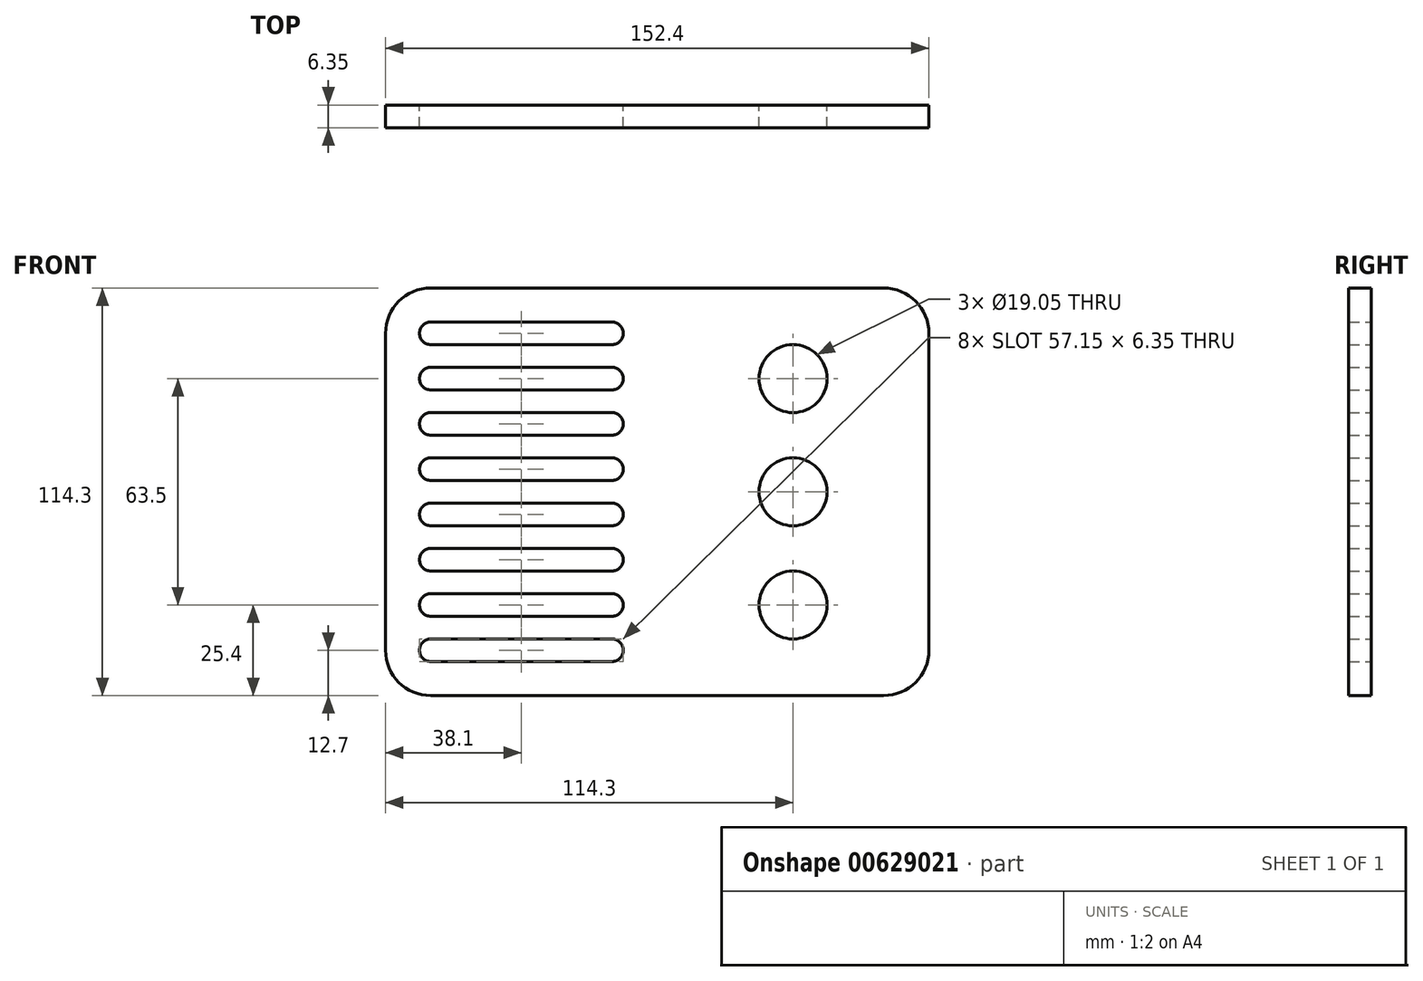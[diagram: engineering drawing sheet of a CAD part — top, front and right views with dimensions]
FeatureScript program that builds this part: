
annotation { "Feature Type Name" : "Feature", "Feature Type Description" : "" }
export const myFeature = defineFeature(function(context is Context, id is Id, definition is map)
    precondition{}
    {
        {
            var Q0;
            Q0=qCreatedBy(makeId("Front.planeOp"),FACE);
            var sketch = newSketch(context, id + "F0", { "sketchPlane" : qUnion([Q0])});
            skLineSegment(sketch, "E0.bottom", {"start": v(12.7, 0) * mm, "end": v(139.7, 0) * mm});
            skLineSegment(sketch, "E0.top", {"start": v(12.7, 114.3) * mm, "end": v(139.7, 114.3) * mm});
            skLineSegment(sketch, "E0.left", {"start": v(0, 12.7) * mm, "end": v(0, 101.6) * mm});
            skLineSegment(sketch, "E0.right", {"start": v(152.4, 12.7) * mm, "end": v(152.4, 101.6) * mm});
            skLineSegment(sketch, "E1.bottom", {"start": v(0, 0) * mm, "end": v(12.7, 0) * mm});
            skLineSegment(sketch, "E1.top", {"start": v(9.52, 12.7) * mm, "end": v(12.7, 12.7) * mm});
            skLineSegment(sketch, "E1.left", {"start": v(0, 0) * mm, "end": v(0, 12.7) * mm});
            skLineSegment(sketch, "E1.right", {"start": v(12.7, 9.53) * mm, "end": v(12.7, 12.7) * mm});
            skLineSegment(sketch, "E2", {"start": v(12.7, 12.7) * mm, "end": v(63.5, 12.7) * mm});
            skArc(sketch, "E3.0.startCap", {"start": v(12.7, 9.53) * mm, "mid": v(9.52, 12.7) * mm, "end": v(12.7, 15.88) * mm});
            skArc(sketch, "E3.0.endCap", {"start": v(63.5, 15.88) * mm, "mid": v(66.67, 12.7) * mm, "end": v(63.5, 9.53) * mm});
            skLineSegment(sketch, "E3.0.left", {"start": v(12.7, 15.88) * mm, "end": v(63.5, 15.88) * mm});
            skLineSegment(sketch, "E3.0.right", {"start": v(12.7, 9.53) * mm, "end": v(63.5, 9.53) * mm});
            skLineSegment(sketch, "E4.0.1.0", {"start": v(12.7, 28.58) * mm, "end": v(63.5, 28.58) * mm});
            skArc(sketch, "E4.0.1.1", {"start": v(63.5, 28.58) * mm, "mid": v(66.67, 25.4) * mm, "end": v(63.5, 22.23) * mm});
            skLineSegment(sketch, "E4.0.1.2", {"start": v(12.7, 22.23) * mm, "end": v(63.5, 22.23) * mm});
            skArc(sketch, "E4.0.1.3", {"start": v(12.7, 22.23) * mm, "mid": v(9.52, 25.4) * mm, "end": v(12.7, 28.58) * mm});
            skLineSegment(sketch, "E4.0.2.0", {"start": v(12.7, 41.28) * mm, "end": v(63.5, 41.28) * mm});
            skArc(sketch, "E4.0.2.1", {"start": v(63.5, 41.27) * mm, "mid": v(66.67, 38.1) * mm, "end": v(63.5, 34.93) * mm});
            skLineSegment(sketch, "E4.0.2.2", {"start": v(12.7, 34.93) * mm, "end": v(63.5, 34.93) * mm});
            skArc(sketch, "E4.0.2.3", {"start": v(12.7, 34.93) * mm, "mid": v(9.52, 38.1) * mm, "end": v(12.7, 41.28) * mm});
            skLineSegment(sketch, "E4.0.3.0", {"start": v(12.7, 53.98) * mm, "end": v(63.5, 53.98) * mm});
            skArc(sketch, "E4.0.3.1", {"start": v(63.5, 53.98) * mm, "mid": v(66.67, 50.8) * mm, "end": v(63.5, 47.63) * mm});
            skLineSegment(sketch, "E4.0.3.2", {"start": v(12.7, 47.63) * mm, "end": v(63.5, 47.63) * mm});
            skArc(sketch, "E4.0.3.3", {"start": v(12.7, 47.63) * mm, "mid": v(9.52, 50.8) * mm, "end": v(12.7, 53.98) * mm});
            skLineSegment(sketch, "E4.0.4.0", {"start": v(12.7, 66.68) * mm, "end": v(63.5, 66.68) * mm});
            skArc(sketch, "E4.0.4.1", {"start": v(63.5, 66.67) * mm, "mid": v(66.67, 63.5) * mm, "end": v(63.5, 60.33) * mm});
            skLineSegment(sketch, "E4.0.4.2", {"start": v(12.7, 60.33) * mm, "end": v(63.5, 60.33) * mm});
            skArc(sketch, "E4.0.4.3", {"start": v(12.7, 60.33) * mm, "mid": v(9.52, 63.5) * mm, "end": v(12.7, 66.68) * mm});
            skLineSegment(sketch, "E4.0.5.0", {"start": v(12.7, 79.38) * mm, "end": v(63.5, 79.38) * mm});
            skArc(sketch, "E4.0.5.1", {"start": v(63.5, 79.38) * mm, "mid": v(66.67, 76.2) * mm, "end": v(63.5, 73.03) * mm});
            skLineSegment(sketch, "E4.0.5.2", {"start": v(12.7, 73.03) * mm, "end": v(63.5, 73.03) * mm});
            skArc(sketch, "E4.0.5.3", {"start": v(12.7, 73.03) * mm, "mid": v(9.52, 76.2) * mm, "end": v(12.7, 79.38) * mm});
            skLineSegment(sketch, "E4.0.6.0", {"start": v(12.7, 92.08) * mm, "end": v(63.5, 92.08) * mm});
            skArc(sketch, "E4.0.6.1", {"start": v(63.5, 92.08) * mm, "mid": v(66.67, 88.9) * mm, "end": v(63.5, 85.73) * mm});
            skLineSegment(sketch, "E4.0.6.2", {"start": v(12.7, 85.73) * mm, "end": v(63.5, 85.73) * mm});
            skArc(sketch, "E4.0.6.3", {"start": v(12.7, 85.73) * mm, "mid": v(9.52, 88.9) * mm, "end": v(12.7, 92.08) * mm});
            skLineSegment(sketch, "E4.0.7.0", {"start": v(12.7, 104.78) * mm, "end": v(63.5, 104.78) * mm});
            skArc(sketch, "E4.0.7.1", {"start": v(63.5, 104.78) * mm, "mid": v(66.67, 101.6) * mm, "end": v(63.5, 98.43) * mm});
            skLineSegment(sketch, "E4.0.7.2", {"start": v(12.7, 98.43) * mm, "end": v(63.5, 98.43) * mm});
            skArc(sketch, "E4.0.7.3", {"start": v(12.7, 98.43) * mm, "mid": v(9.52, 101.6) * mm, "end": v(12.7, 104.78) * mm});
            skLineSegment(sketch, "E4.direction1", {"start": v(12.7, 15.88) * mm, "end": v(38.1, 15.88) * mm, "construction": true});
            skLineSegment(sketch, "E4.direction2", {"start": v(12.7, 15.88) * mm, "end": v(12.7, 28.58) * mm, "construction": true});
            skLineSegment(sketch, "E5.bottom", {"start": v(152.4, 0) * mm, "end": v(114.3, 0) * mm});
            skLineSegment(sketch, "E5.top", {"start": v(123.83, 25.4) * mm, "end": v(114.3, 25.4) * mm});
            skLineSegment(sketch, "E5.left", {"start": v(152.4, 0) * mm, "end": v(152.4, 25.4) * mm});
            skLineSegment(sketch, "E5.right", {"start": v(114.3, 15.87) * mm, "end": v(114.3, 25.4) * mm});
            skCircle(sketch, "E6", {"center": v(114.3, 25.4) * mm, "radius": 9.53 * mm});
            skCircle(sketch, "E7.0.1.0", {"center": v(114.3, 57.15) * mm, "radius": 9.53 * mm});
            skCircle(sketch, "E7.0.2.0", {"center": v(114.3, 88.9) * mm, "radius": 9.53 * mm});
            skLineSegment(sketch, "E7.direction1", {"start": v(114.3, 25.4) * mm, "end": v(123.83, 25.4) * mm, "construction": true});
            skLineSegment(sketch, "E7.direction2", {"start": v(114.3, 25.4) * mm, "end": v(114.3, 57.15) * mm, "construction": true});
            skPoint(sketch, "E8.visualSharp", {"position": v(0, 114.3) * mm});
            skArc(sketch, "E8.filletArc", {"start": v(12.7, 114.3) * mm, "mid": v(3.72, 110.58) * mm, "end": v(0, 101.6) * mm});
            skPoint(sketch, "E9.visualSharp", {"position": v(0, 0) * mm});
            skArc(sketch, "E9.filletArc", {"start": v(0, 12.7) * mm, "mid": v(3.72, 3.72) * mm, "end": v(12.7, 0) * mm});
            skPoint(sketch, "E10.visualSharp", {"position": v(152.4, 114.3) * mm});
            skArc(sketch, "E10.filletArc", {"start": v(152.4, 101.6) * mm, "mid": v(148.68, 110.58) * mm, "end": v(139.7, 114.3) * mm});
            skPoint(sketch, "E11.visualSharp", {"position": v(152.4, 0) * mm});
            skArc(sketch, "E11.filletArc", {"start": v(139.7, 0) * mm, "mid": v(148.68, 3.72) * mm, "end": v(152.4, 12.7) * mm});
            skSolve(sketch);
        }
        {
            var Q0;
            {var subQ4=sQuery(id+"F0.wireOp",EDGE,"E0.bottom");Q0=makeQuery(id+"F0.imprint","IMPRINT",FACE,{"disambiguationData":[TD([[makeQuery(id+"F0.imprint","IMPRINT",EDGE,{"derivedFrom":subQ4}),1.0]])]});}
            extrude(context, id + "F1", {"entities" : qUnion([Q0]), "depth" : 6.35 * mm, "offsetDistance" : 25.4 * mm});
        }
    });
